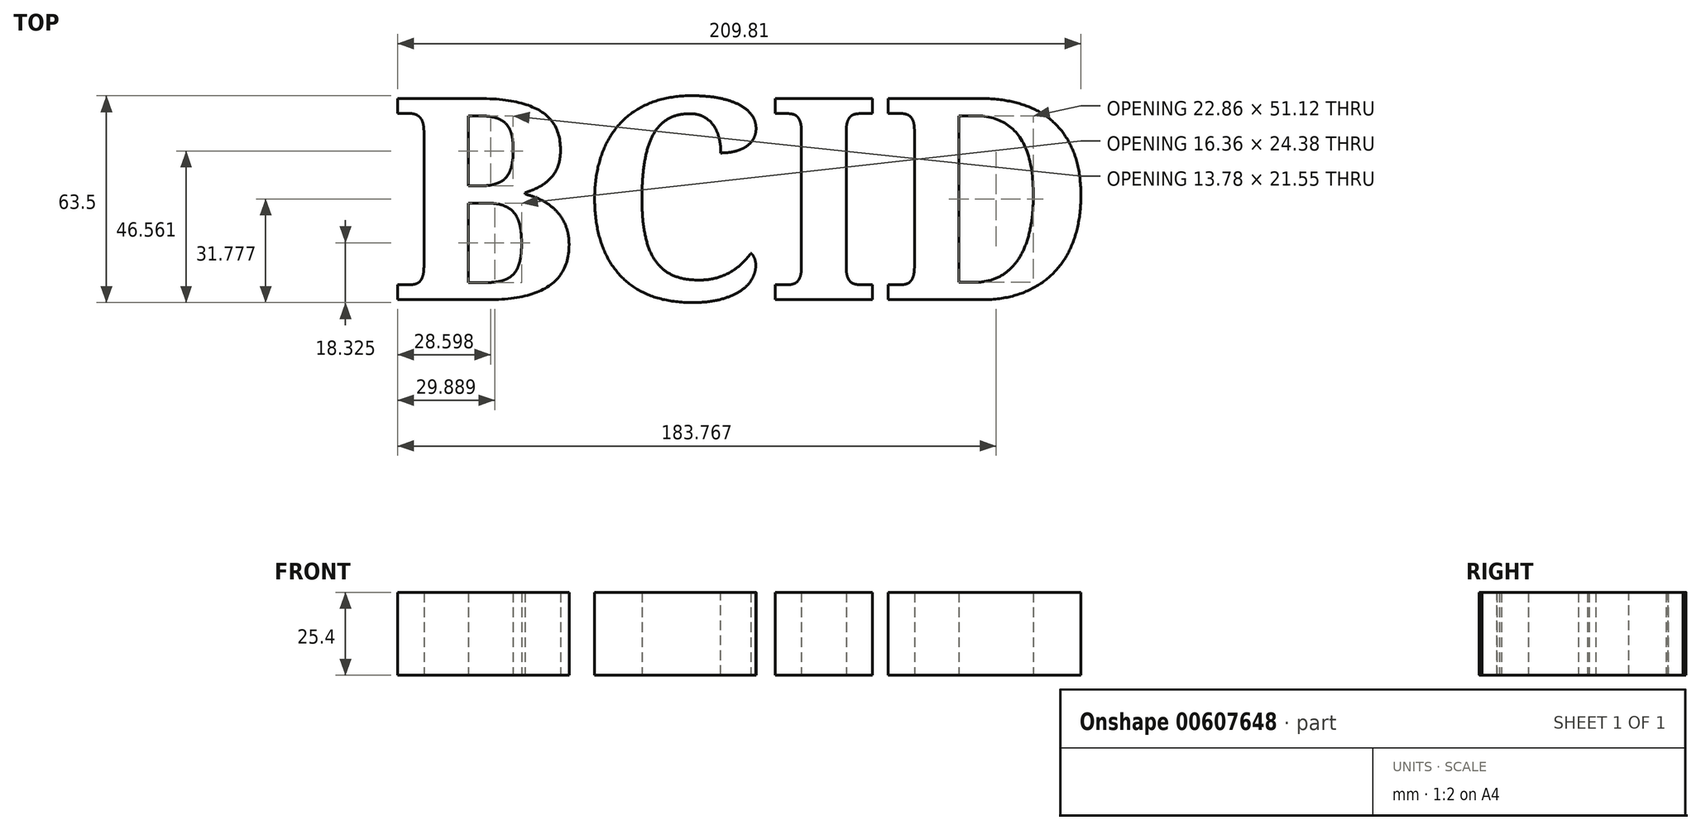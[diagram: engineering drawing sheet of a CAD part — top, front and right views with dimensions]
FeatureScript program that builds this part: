
annotation { "Feature Type Name" : "Feature", "Feature Type Description" : "" }
export const myFeature = defineFeature(function(context is Context, id is Id, definition is map)
    precondition{}
    {
        {
            var Q0;
            Q0=qCreatedBy(makeId("Top.planeOp"),FACE);
            var sketch = newSketch(context, id + "F0", { "sketchPlane" : qUnion([Q0])});
            skText(sketch, "E0", { "text": "BCID", "fontName": "NotoSerif-Bold.ttf"});
            const initialGuessF0  = {"E0": [-0.06147, -0.027, 1, 0, 0.0623]};
            skSetInitialGuess(sketch, initialGuessF0);
            skSolve(sketch);
        }
        {
            var Q0;
            Q0 = qSketchRegion(id + "F0", true);
            extrude(context, id + "F1", {"entities" : qUnion([Q0]), "depth" : 25.4 * mm, "offsetDistance" : 25.4 * mm});
        }
    });
